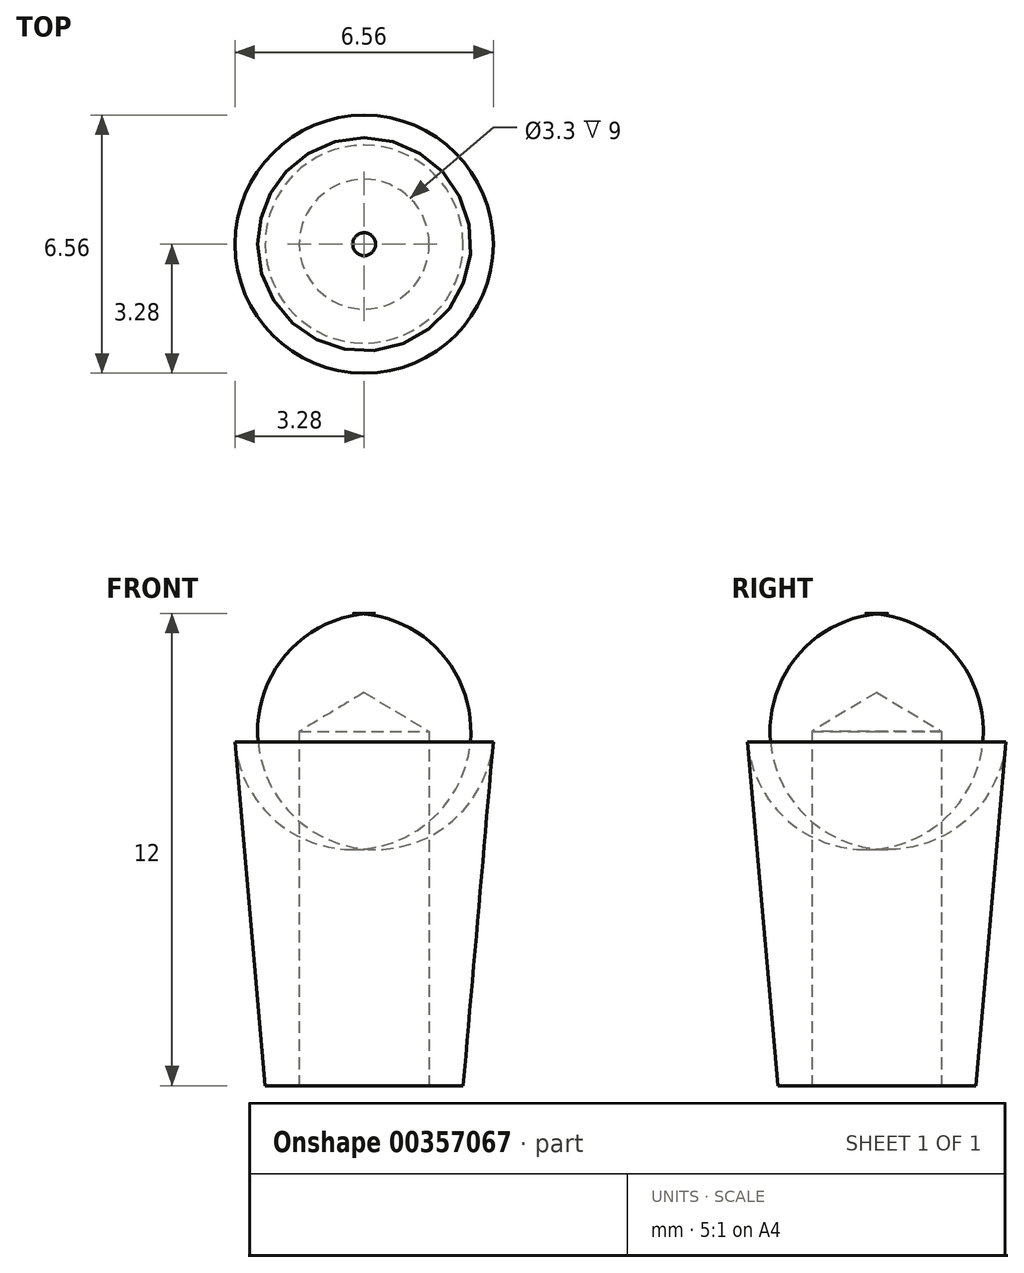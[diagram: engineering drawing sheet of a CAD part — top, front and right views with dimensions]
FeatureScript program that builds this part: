
annotation { "Feature Type Name" : "Feature", "Feature Type Description" : "" }
export const myFeature = defineFeature(function(context is Context, id is Id, definition is map)
    precondition{}
    {
        {
            var Q0;
            Q0=qCreatedBy(makeId("Top.planeOp"),FACE);
            var sketch = newSketch(context, id + "F0", { "sketchPlane" : qUnion([Q0])});
            skCircle(sketch, "E0", {"center": v(0, 0) * mm, "radius": 2.51 * mm});
            skSolve(sketch);
        }
        {
            var Q0;
            Q0=makeQuery(id+"F0.imprint","IMPRINT",FACE,{"disambiguationData":[TD([[makeQuery(id+"F0.imprint","IMPRINT",EDGE,{"derivedFrom":sQuery(id+"F0.wireOp",EDGE,"E0")}),1.0]])]});
            extrude(context, id + "F1", {"entities" : qUnion([Q0]), "depth" : 12 * mm, "hasDraft" : true, "draftAngle" : 5 * degree});
        }
        {
            var Q0;
            Q0=makeQuery(id+"F1.opExtrude","CAP_FACE",FACE,{"disambiguationData":[OSD([sQuery(id+"F0.wireOp",EDGE,"E0")])],"isStart":false});
            fillet(context, id + "F2", {"entities" : qUnion([Q0]), "radius" : 3 * mm, "tangentPropagation" : true, "allowEdgeOverflow" : false});
        }
        {
            var Q0;
            Q0=qCreatedBy(makeId("Top.planeOp"),FACE);
            var sketch = newSketch(context, id + "F3", { "sketchPlane" : qUnion([Q0])});
            skCircle(sketch, "E1", {"center": v(0, 0) * mm, "radius": 1.59 * mm});
            skSolve(sketch);
        }
        {
            var Q0;
            Q0=sQuery(id+"F3.wireOp",VERTEX,"E1.center");
            var Q1;
            Q1=makeQuery(id+"F1.opExtrude","SWEPT_BODY",BODY,{"disambiguationData":[OSD([sQuery(id+"F0.wireOp",EDGE,"E0")])]});
            hole(context, id + "F4", {"style" : HoleStyle.SIMPLE, "endStyle" : HoleEndStyle.BLIND, "oppositeDirection" : true, "holeDiameter" : 3.3 * mm, "holeDepth" : 9 * mm, "isTappedThrough" : true, "tappedDepth" : 12 * mm, "tapClearance" : 3, "locations" : qUnion([Q0]), "scope" : qUnion([Q1])});
        }
    });
